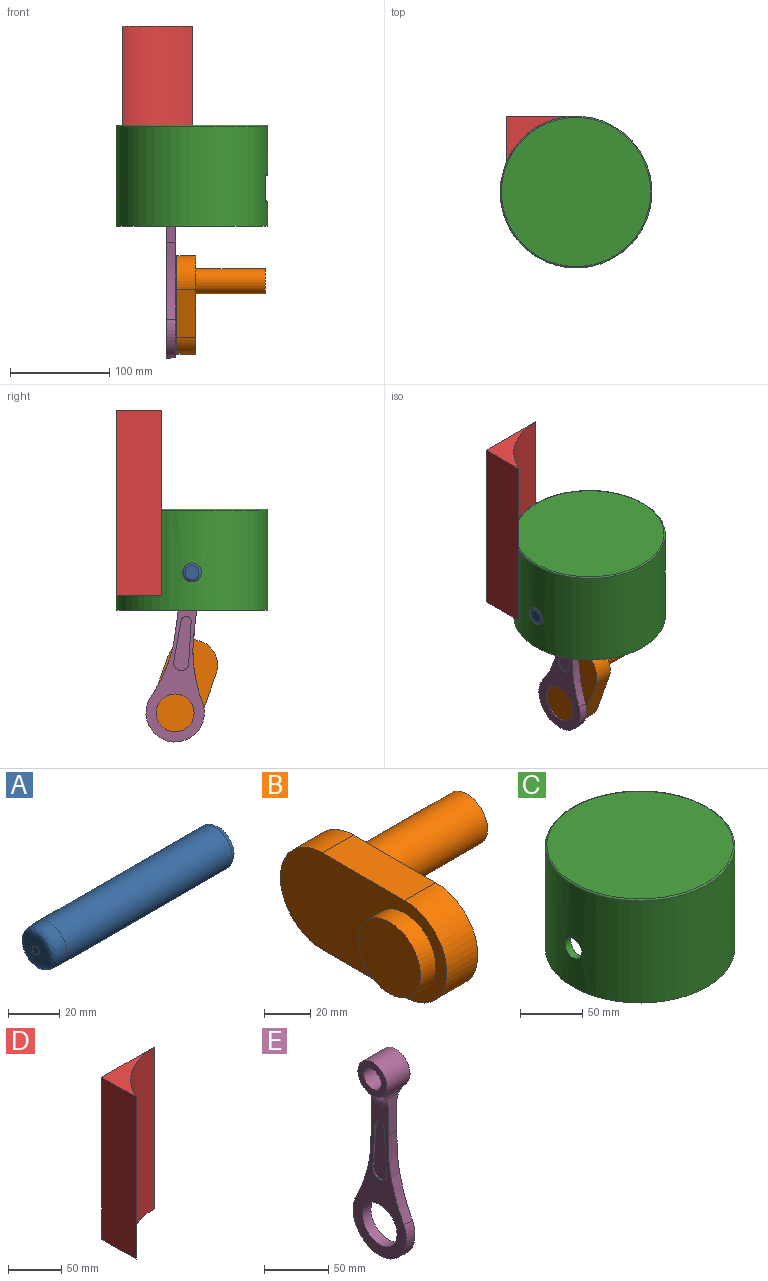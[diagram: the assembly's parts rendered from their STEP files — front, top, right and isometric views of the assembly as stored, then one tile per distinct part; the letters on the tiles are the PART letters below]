
ASSEMBLY  parts=5 mates=5
PART A: 5 faces, bbox 101.6x20.6x20.6 mm
  f0: cylinder r=9.53mm len=91.44mm, axis (1,0,0), area 5472.4mm2, adj f3,f4
  f1: plane 3.81x3.81mm, normal (-1,0,0), area 11.4mm2, adj f4
  f2: plane 13.97x13.97mm, normal (1,0,0), area 153.3mm2, adj f3
  f3: torus R=6.99mm, axis (1,0,0), area 215.6mm2, adj f0,f2
  f4: bspline ~19.05x19.05mm, area 631.1mm2, adj f0,f1
PART B: 10 faces, bbox 98.3x102.2x51.4 mm
  f0: cylinder r=19.05mm len=38.1mm, axis (1,0,0), area 1131mm2, adj f1,f7
  f1: plane 38.1x38.1mm, normal (-1,0,0), area 1140.1mm2, adj f0
  f2: cylinder r=25.72mm len=51.44mm, axis (-1,0,0), area 1539.1mm2, adj f3,f5,f6,f7
  f3: plane 50.8x19.05mm, normal (0,0,-1), area 967.7mm2, adj f2,f4,f6,f7
  f4: cylinder r=25.72mm len=51.44mm, axis (-1,0,0), area 1539.1mm2, adj f3,f5,f6,f7
  f5: plane 50.8x19.05mm, normal (0,0,1), area 967.7mm2, adj f2,f4,f6,f7
  f6: plane 102.24x51.44mm, normal (1,0,0), area 4184.1mm2, adj f2,f3,f4,f5,f8
  f7: plane 102.24x51.44mm, normal (-1,0,0), area 3550.7mm2, adj f0,f2,f3,f4,f5
  f8: cylinder r=12.7mm len=69.85mm, axis (-1,0,0), area 5573.8mm2, adj f6,f9
  f9: plane 25.4x25.4mm, normal (1,0,0), area 506.7mm2, adj f8
PART C: 16 faces, bbox 165x165x101.6 mm
  f0: cylinder r=76.2mm len=152.4mm, axis (0,0,1), area 46650mm2, adj f3,f6,f10,f11,f13,f14,f15
  f1: cylinder r=9.53mm len=19.05mm, axis (1,0,0), area 171.5mm2, adj f4,f9
  f2: plane 149.86x149.86mm, normal (0,0,1), area 17638.5mm2, adj f15
  f3: plane 152.4x152.4mm, normal (0,0,-1), area 2913.6mm2, adj f0,f4
  f4: cylinder r=69.85mm len=139.7mm, axis (0,0,1), area 39561.3mm2, adj f1,f3,f5,f6
  f5: plane 139.7x139.7mm, normal (0,0,-1), area 15327.9mm2, adj f4
  f6: cylinder r=9.53mm len=19.05mm, axis (1,0,0), area 381.7mm2, adj f0,f4
  f7: plane 38.69x25.07mm, normal (1,0,0), area 570mm2, adj f8,f9,f10,f11,f12,f13
  f8: plane 27.47x1.27mm, normal (0,0,1), area 23.3mm2, adj f7,f10
  f9: torus R=10.79mm, axis (1,0,0), area 125.2mm2, adj f1,f7
  f10: torus R=74.93mm, axis (0,0,1), area 70.7mm2, adj f0,f7,f8,f11,f13
  f11: cylinder r=1.27mm len=25.4mm, axis (0,0,1), area 8.4mm2, adj f0,f7,f10,f14
  f12: cylinder r=1.27mm len=38.69mm, axis (0,-1,0), area 59mm2, adj f7,f14
  f13: cylinder r=1.27mm len=25.4mm, axis (0,0,1), area 8.4mm2, adj f0,f7,f10,f14
  f14: bspline ~39.35x2.64mm, area 60.9mm2, adj f0,f11,f12,f13
  f15: torus R=74.93mm, axis (0,0,1), area 949.3mm2, adj f0,f2
PART D: 5 faces, bbox 69.9x45.7x186.7 mm
  f0: plane 186.72x45.75mm, normal (-1,0,0), area 8541.6mm2, adj f1,f2,f3,f4
  f1: plane 186.72x69.85mm, normal (0,1,0), area 13042.1mm2, adj f0,f2,f3,f4
  f2: cylinder r=76.2mm len=186.72mm, axis (0,0,-1), area 16499.3mm2, adj f0,f1,f3,f4
  f3: plane 69.85x45.75mm, normal (0,0,1), area 892.2mm2, adj f0,f1,f2
  f4: plane 69.85x45.75mm, normal (0,0,-1), area 892.2mm2, adj f0,f1,f2
PART E: 26 faces, bbox 35.2x61.2x187.8 mm
  f0: cylinder r=9.53mm len=25.4mm, axis (-1,0,0), area 1520.1mm2, adj f2,f3
  f1: cylinder r=15.88mm len=31.75mm, axis (-1,0,0), area 1829.5mm2, adj f2,f3,f8,f11
  f2: plane 31.75x31.75mm, normal (1,0,0), area 506.7mm2, adj f0,f1,f10
  f3: plane 31.75x31.75mm, normal (-1,0,0), area 506.7mm2, adj f0,f1,f9
  f4: plane 35.2x14.16mm, normal (0,-1,0), area 340mm2, adj f6,f7,f8,f9,f10,f14
  f5: plane 35.2x14.16mm, normal (0,1,0), area 340mm2, adj f6,f7,f9,f10,f11,f15
  f6: plane 145.49x58.64mm, normal (1,0,0), area 2910.8mm2, adj f4,f5,f10,f12,f13,f14,f15,f21
  f7: plane 145.49x58.64mm, normal (-1,0,0), area 2910.8mm2, adj f4,f5,f9,f12,f13,f14,f15,f16
  f8: cylinder r=12.7mm len=25.4mm, axis (-1,0,0), area 173.8mm2, adj f1,f4,f9,f10
  f9: torus R=27.67mm, axis (-1,0,0), area 323.1mm2, adj f3,f4,f5,f7,f8,f11
  f10: torus R=27.67mm, axis (-1,0,0), area 323.1mm2, adj f2,f4,f5,f6,f8,f11
  f11: cylinder r=12.7mm len=25.4mm, axis (-1,0,0), area 173.8mm2, adj f1,f5,f9,f10
  f12: cylinder r=29.31mm len=58.63mm, axis (-1,0,0), area 1115mm2, adj f6,f7,f14,f15
  f13: cylinder r=19.05mm len=38.1mm, axis (-1,0,0), area 1129.5mm2, adj f6,f7
  f14: bspline ~76.44x17.27mm, area 748.3mm2, adj f4,f6,f7,f12
  f15: bspline ~76.44x17.27mm, area 748.3mm2, adj f5,f6,f7,f12
  f16: plane 41.88x2.53mm, normal (0,1,-0.06), area 53.3mm2, adj f7,f17,f19,f20
  f17: cylinder r=5.09mm len=10.16mm, axis (-1,0,0), area 19.5mm2, adj f7,f16,f18,f20
  f18: plane 41.88x2.53mm, normal (0,-1,-0.06), area 53.3mm2, adj f7,f17,f19,f20
  f19: cylinder r=7.62mm len=15.25mm, axis (-1,0,0), area 31.6mm2, adj f7,f16,f18,f20
  f20: plane 54.75x15.25mm, normal (-1,0,0), area 667.4mm2, adj f16,f17,f18,f19
  f21: plane 41.88x2.53mm, normal (0,1,-0.06), area 53.3mm2, adj f6,f22,f24,f25
  f22: cylinder r=7.62mm len=15.25mm, axis (1,0,0), area 31.6mm2, adj f6,f21,f23,f25
  f23: plane 41.88x2.53mm, normal (0,-1,-0.06), area 53.3mm2, adj f6,f22,f24,f25
  f24: cylinder r=5.09mm len=10.16mm, axis (1,0,0), area 19.5mm2, adj f6,f21,f23,f25
  f25: plane 54.75x15.25mm, normal (1,0,0), area 667.4mm2, adj f21,f22,f23,f24
PLACE A rot(axis=(0,-1,0),180deg) t=(11.6,-38.75,-200.25)mm
PLACE B rot(axis=(1,0,0),109.5deg) t=(-8.3,-215.7,-346.76)mm
PLACE C rot(axis=(0,0,1),0deg) t=(11.65,-38.75,-73.25)mm
PLACE D t=(11.65,-38.75,-58.67)mm fixed
PLACE E rot(axis=(1,0,0),6.9deg) t=(-9.22,-46.33,-73.7)mm
MATE fastened A.f0 <-> C.f1  axis (-1,0,0) through (-64.6,-38.75,-136.75)mm
MATE cylindrical E.f12 <-> B.f0  axis (-1,0,0) through (-9.22,-21.77,-277.99)mm
MATE revolute E.f0 <-> A.f0  axis (-1,0,0) through (-9.22,-38.75,-136.75)mm
MATE cylindrical D.f2 <-> C.f0  axis (0,0,-1) through (11.65,-38.75,-66.91)mm
MATE slider C.f0 <-> D.f2  axis (0,0,1) through (11.65,-38.75,-174.85)mm
